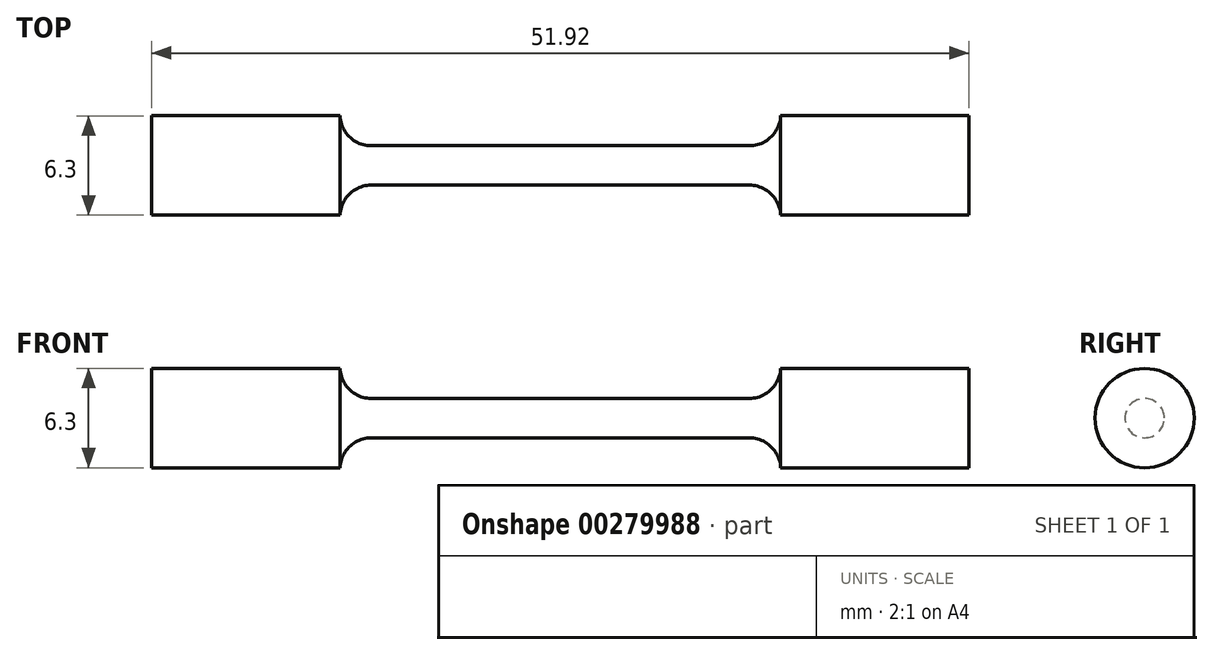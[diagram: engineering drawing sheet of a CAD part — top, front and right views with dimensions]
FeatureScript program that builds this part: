
annotation { "Feature Type Name" : "Feature", "Feature Type Description" : "" }
export const myFeature = defineFeature(function(context is Context, id is Id, definition is map)
    precondition{}
    {
        {
            var Q0;
            Q0=qCreatedBy(makeId("Front.planeOp"),FACE);
            var sketch = newSketch(context, id + "F0", { "sketchPlane" : qUnion([Q0])});
            skLineSegment(sketch, "E0", {"start": v(0, 1.25) * mm, "end": v(12, 1.25) * mm});
            skArc(sketch, "E1", {"start": v(12, 1.25) * mm, "mid": v(13.38, 1.8) * mm, "end": v(14, 3.15) * mm});
            skLineSegment(sketch, "E2", {"start": v(14, 3.15) * mm, "end": v(25.96, 3.15) * mm});
            skLineSegment(sketch, "E3", {"start": v(25.96, 3.15) * mm, "end": v(25.96, 0) * mm});
            skLineSegment(sketch, "E4.MirrorCS", {"start": v(0, 1.25) * mm, "end": v(-12, 1.25) * mm});
            skLineSegment(sketch, "E5.MirrorCS", {"start": v(-25.96, 3.15) * mm, "end": v(-25.96, 0) * mm});
            skLineSegment(sketch, "E6.MirrorCS", {"start": v(-14, 3.15) * mm, "end": v(-25.96, 3.15) * mm});
            skArc(sketch, "E7.MirrorCS", {"start": v(-12, 1.25) * mm, "mid": v(-13.38, 1.8) * mm, "end": v(-14, 3.15) * mm});
            skLineSegment(sketch, "E8", {"start": v(-25.96, 0) * mm, "end": v(25.96, 0) * mm});
            skSolve(sketch);
        }
        {
            var Q0;
            Q0 = qSketchRegion(id + "F0", true);
            var Q1;
            Q1=sQuery(id+"F0.wireOp",EDGE,"E8");
            revolve(context, id + "F1", {"entities" : qUnion([Q0]), "axis" : qUnion([Q1]), "revolveType" : RevolveType.FULL});
        }
    });
